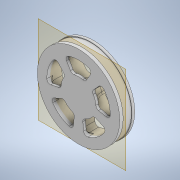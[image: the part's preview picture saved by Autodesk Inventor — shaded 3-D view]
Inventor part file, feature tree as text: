
AUTODESK INVENTOR PART (.ipt)
format: ipt  version: 2020.3 (Build 243373000, 373)  size: 858,624 bytes
history: native  units: in
note: dims shown in document units (in); Inventor stores cm internally (conversion verified against a paired STEP export)
features: extrude x5, sketch x5, other x3, plane x1
ambient origin geometry x8: Origin, YZ Plane, XZ Plane, XY Plane, X Axis, Y Axis, Z Axis, Center Point
bodies: Solid1 (feature_tree)
feature tree (14):
  other  "wheel 3.0001.ipt"
  extrude  "Extrusion1"  Depth=0.3937in TaperAngle=0.0deg
  plane  "Work Plane1"
  extrude  "Extrusion2"  Depth=2.375in
  extrude  "Extrusion3"  Depth=1.0in TaperAngle=0.0deg
  extrude  "Extrusion4"  Depth=0.265in TaperAngle=0.0deg
  extrude  "Extrusion5"  Depth=0.5in
  other  "Solid1::wheel 3.0001.ipt"
  other  "TaggingFeature1"
  sketch  "Sketch1"  dims[d0=0.3937in d1=1.0in d2=0.0in]
  sketch  "Sketch5"  dims[d4=-0.102in d5=2.375in]
  sketch  "Sketch6"  dims[d6=0.264in d7=0.0in d8=1.0in d9=0.0in]
  sketch  "Sketch7"  dims[d10=2.435in d11=0.265in d12=0.0in]
  sketch  "Sketch8"  dims[d13=1.0in d14=0.0in d3=0.5in]
